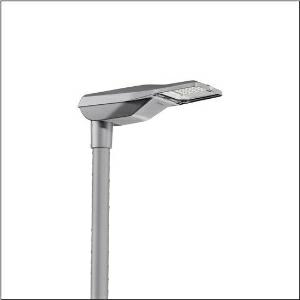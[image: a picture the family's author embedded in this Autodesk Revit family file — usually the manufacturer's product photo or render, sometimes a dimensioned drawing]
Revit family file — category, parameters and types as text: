
# Revit family: streetlight_sl_21_iq_micro___st0_8a_5xe1c41g08cb_fbf2
name_source: partatom
category: Lighting Fixtures
units: mm (PartAtom-declared; Revit-internal decimal feet)

## family parameters
Cut with Voids When Loaded = No
Host = Face
Light Source = No
Part Type = Normal
Room Calculation Point = No
Round Connector Dimension = Use Diameter
Shared = No

## types (1)
- --- (1 x LED, 2980 lm, 19.4 W, 4000K)
    Apparent Load = 19 VA
    CIE Flux Codes = 38 75 97 100 100
    Color Rendering = 70
    Color Temperature = 4000K
    Default Elevation = 1800 mm
    Description = Streetlight SL 21 iQ micro, mast luminaire, primary light control with lens, of PMMA, primary optical cover: cover, of toughened safety glass, transparent, light distribution: ST0.8a, light emission: direct distribution, primary light characteristic: asymmetric, installation type: post-top, side-entry, LED, High Power LED, rated luminous flux: 2.980lm, luminous efficacy: 154lm/W, light colour: 740, colour temperature: 4000K, control gear: iQ Street-Remote, control: Street-Remote, Auto-Match, Temp-Guard, Lumen-Switch, Night-Set, Smart-Wire, Light-Fading, Desk-Remote (wireless, voltage-free reading and setting of iQ features in the workshop via application-optimized NFC function/RFID function), optimised constant luminous flux control (CLO 2.0), pre-setting: linear dimming characteristic, mains connection: 220..240V, AC, 50/60Hz, start of lifetime: 19W, end of service life: 20W, reduction: 10W, luminaire housing, of diecast aluminium, powder-coated, Siteco® metallic grey (DB 702S), corrosivity category C5 mid according to DIN EN ISO 12944, please order mast flange separately, inclination adjustable: 0°, 5°, 10°, 15°, sealing non-destructively replaceable, multi-level sealing system, length: 528mm, width: 235mm, height: 110mm, mast flange for spigot size: 42mm (side-entry): 5XC10008XM4, 60/48mm (side-entry/post-top): 5XC10108XM2, 76/60mm (side-entry/post-top): 5XC10108XM1, protection rating (complete): IP66, insulation class (complete): insulation class II (safety insulation), certification: CE, ENEC, ENEC+, VDE, impact resistance: IK10, permissible operating ambient temperature for outdoor applications: -40..+50°C, standard-compliant lighting for roads and squares, packaging unit: 1 piece

Light Distribution: ST0.8a
    Height = 110 mm
    Lamp = 1 x LED
    Lamp Light Flux = 2980 lm
    Lamp Power = 19.4 W
    Lamp count = 1
    Length = 528 mm
    Luminous efficacy = 154 lm/W
    Manufacturer = Siteco
    ModVariant = No
    Model = 5XE1C41G08CB
    Number of Poles = 1
    OnlyDefault = Yes
    Power Factor = 1
    Product Name = Streetlight SL 21 iQ micro | ST0.8a
    Product group = mast luminaire | pylon top
    ProductGroupID = 6100
    Protection Class = Protection class II
    Protection Degree = IP 66
    RLX_Detail_Level = 1
    RLX_Emergency_Light_Flux = 0 lm
    RLX_Emergency_Type = 0
    RLX_Emergency_Type_DB = No
    RlxData = <blob elided: 98553 chars, md5=889cd402>
    Socket = socket
    Standby Power = 0 W
    System Light Flux = 2980 lm
    System Power = 19 W
    Type Comments = factory setting: luminous flux: 100 % | dim-lin: 254 | 387 mA
    Type Image = l_1006881.jpg
    URL = http://relux.com
    VarID = @adj_159835
    Voltage = 0 V
    Weight = 0.00 kg
    Width = 235 mm

## geometry (parser evidence)
native form markers: Blend x4, Sweep x11
no freeform markers — native parametric forms only
